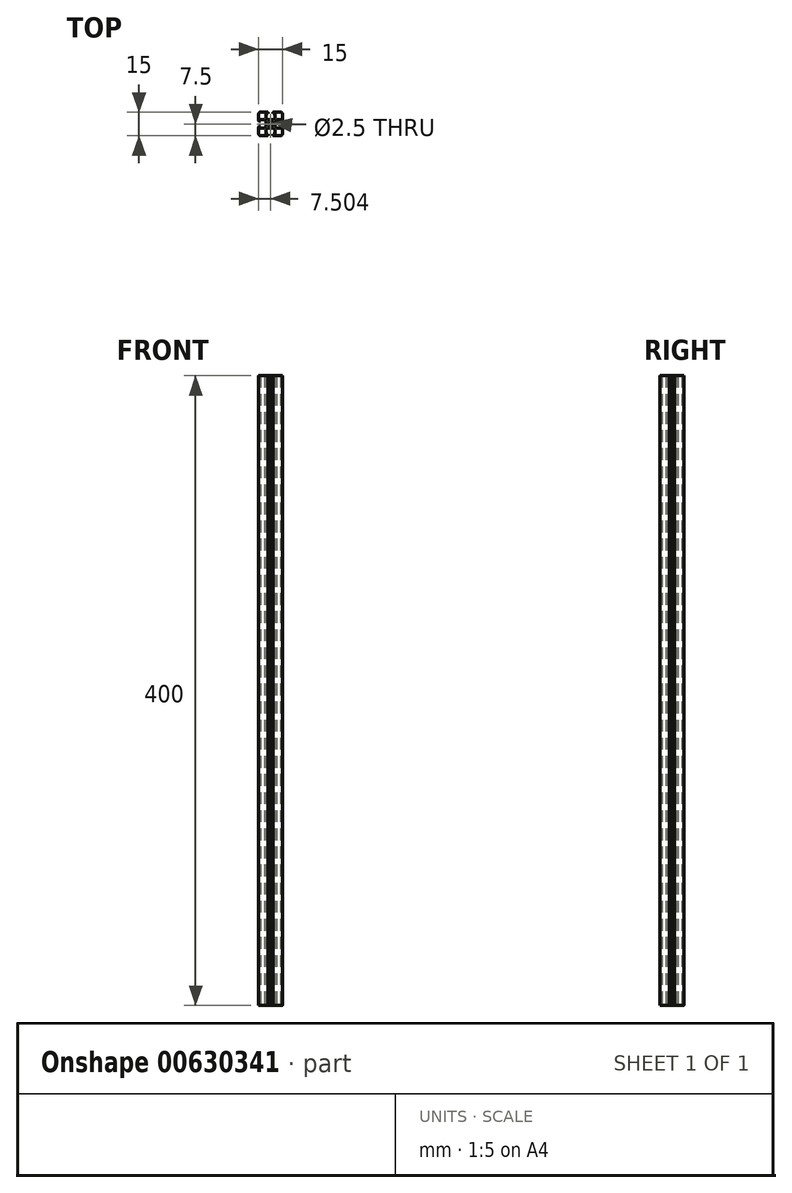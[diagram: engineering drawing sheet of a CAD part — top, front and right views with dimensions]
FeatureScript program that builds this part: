
annotation { "Feature Type Name" : "Feature", "Feature Type Description" : "" }
export const myFeature = defineFeature(function(context is Context, id is Id, definition is map)
    precondition{}
    {
        {
            var Q0;
            Q0=qCreatedBy(makeId("Top.planeOp"),FACE);
            var sketch = newSketch(context, id + "F0", { "sketchPlane" : qUnion([Q0])});
            skLineSegment(sketch, "E0", {"start": v(-5.54, -0.25) * mm, "end": v(-2.91, -0.25) * mm});
            skLineSegment(sketch, "E1", {"start": v(-4.23, -1.56) * mm, "end": v(-4.23, 1.06) * mm});
            skLineSegment(sketch, "E2", {"start": v(-11.73, 6.25) * mm, "end": v(-11.73, 1.75) * mm});
            skArc(sketch, "E3", {"start": v(-11.73, 1.75) * mm, "mid": v(-11.64, 1.54) * mm, "end": v(-11.43, 1.45) * mm});
            skLineSegment(sketch, "E4", {"start": v(-11.43, 1.45) * mm, "end": v(-10.63, 1.45) * mm});
            skLineSegment(sketch, "E5", {"start": v(-10.63, 1.45) * mm, "end": v(-10.63, 2.6) * mm});
            skLineSegment(sketch, "E6", {"start": v(-10.63, 2.6) * mm, "end": v(-8.03, 2.6) * mm});
            skLineSegment(sketch, "E7", {"start": v(-8.03, 2.6) * mm, "end": v(-7.03, 1.6) * mm});
            skLineSegment(sketch, "E8", {"start": v(-7.03, 1.6) * mm, "end": v(-7.03, 0.27) * mm});
            skLineSegment(sketch, "E9", {"start": v(-7.03, 0.27) * mm, "end": v(-6.73, -0.25) * mm});
            skLineSegment(sketch, "E10", {"start": v(-6.73, -0.25) * mm, "end": v(-7.03, -0.77) * mm});
            skLineSegment(sketch, "E11", {"start": v(-7.03, -0.77) * mm, "end": v(-7.03, -2.1) * mm});
            skLineSegment(sketch, "E12", {"start": v(-7.03, -2.1) * mm, "end": v(-8.03, -3.1) * mm});
            skLineSegment(sketch, "E13", {"start": v(-8.03, -3.1) * mm, "end": v(-10.63, -3.1) * mm});
            skLineSegment(sketch, "E14", {"start": v(-10.63, -3.1) * mm, "end": v(-10.63, -1.95) * mm});
            skLineSegment(sketch, "E15", {"start": v(-10.63, -1.95) * mm, "end": v(-11.43, -1.95) * mm});
            skArc(sketch, "E16", {"start": v(-11.43, -1.95) * mm, "mid": v(-11.64, -2.04) * mm, "end": v(-11.73, -2.25) * mm});
            skLineSegment(sketch, "E17", {"start": v(-11.73, -2.25) * mm, "end": v(-11.73, -6.75) * mm});
            skArc(sketch, "E18", {"start": v(-11.73, -6.75) * mm, "mid": v(-11.43, -7.46) * mm, "end": v(-10.73, -7.75) * mm});
            skLineSegment(sketch, "E19", {"start": v(-10.73, -7.75) * mm, "end": v(-6.23, -7.75) * mm});
            skArc(sketch, "E20", {"start": v(-6.23, -7.75) * mm, "mid": v(-6.01, -7.66) * mm, "end": v(-5.93, -7.45) * mm});
            skLineSegment(sketch, "E21", {"start": v(-5.93, -7.45) * mm, "end": v(-5.93, -6.65) * mm});
            skLineSegment(sketch, "E22", {"start": v(-5.93, -6.65) * mm, "end": v(-7.08, -6.65) * mm});
            skLineSegment(sketch, "E23", {"start": v(-7.08, -6.65) * mm, "end": v(-7.08, -4.05) * mm});
            skLineSegment(sketch, "E24", {"start": v(-7.08, -4.05) * mm, "end": v(-6.08, -3.05) * mm});
            skLineSegment(sketch, "E25", {"start": v(-6.08, -3.05) * mm, "end": v(-4.75, -3.05) * mm});
            skLineSegment(sketch, "E26", {"start": v(-4.75, -3.05) * mm, "end": v(-4.23, -2.75) * mm});
            skLineSegment(sketch, "E27", {"start": v(-4.23, -2.75) * mm, "end": v(-3.7, -3.05) * mm});
            skLineSegment(sketch, "E28", {"start": v(-3.7, -3.05) * mm, "end": v(-2.38, -3.05) * mm});
            skLineSegment(sketch, "E29", {"start": v(-2.38, -3.05) * mm, "end": v(-1.38, -4.05) * mm});
            skLineSegment(sketch, "E30", {"start": v(-1.38, -4.05) * mm, "end": v(-1.38, -6.65) * mm});
            skLineSegment(sketch, "E31", {"start": v(-1.38, -6.65) * mm, "end": v(-2.53, -6.65) * mm});
            skLineSegment(sketch, "E32", {"start": v(-2.53, -6.65) * mm, "end": v(-2.53, -7.45) * mm});
            skArc(sketch, "E33", {"start": v(-2.53, -7.45) * mm, "mid": v(-2.44, -7.66) * mm, "end": v(-2.23, -7.75) * mm});
            skLineSegment(sketch, "E34", {"start": v(-2.23, -7.75) * mm, "end": v(2.27, -7.75) * mm});
            skArc(sketch, "E35", {"start": v(2.27, -7.75) * mm, "mid": v(2.98, -7.46) * mm, "end": v(3.27, -6.75) * mm});
            skLineSegment(sketch, "E36", {"start": v(3.27, -6.75) * mm, "end": v(3.27, -2.25) * mm});
            skArc(sketch, "E37", {"start": v(3.27, -2.25) * mm, "mid": v(3.19, -2.04) * mm, "end": v(2.97, -1.95) * mm});
            skLineSegment(sketch, "E38", {"start": v(2.97, -1.95) * mm, "end": v(2.17, -1.95) * mm});
            skLineSegment(sketch, "E39", {"start": v(2.17, -1.95) * mm, "end": v(2.17, -3.1) * mm});
            skLineSegment(sketch, "E40", {"start": v(2.17, -3.1) * mm, "end": v(-0.43, -3.1) * mm});
            skLineSegment(sketch, "E41", {"start": v(-0.43, -3.1) * mm, "end": v(-1.43, -2.1) * mm});
            skLineSegment(sketch, "E42", {"start": v(-1.43, -2.1) * mm, "end": v(-1.43, -0.77) * mm});
            skLineSegment(sketch, "E43", {"start": v(-1.43, -0.77) * mm, "end": v(-1.73, -0.25) * mm});
            skLineSegment(sketch, "E44", {"start": v(-1.73, -0.25) * mm, "end": v(-1.43, 0.27) * mm});
            skLineSegment(sketch, "E45", {"start": v(-1.43, 0.27) * mm, "end": v(-1.43, 1.6) * mm});
            skLineSegment(sketch, "E46", {"start": v(-1.43, 1.6) * mm, "end": v(-0.43, 2.6) * mm});
            skLineSegment(sketch, "E47", {"start": v(-0.43, 2.6) * mm, "end": v(2.17, 2.6) * mm});
            skLineSegment(sketch, "E48", {"start": v(2.17, 2.6) * mm, "end": v(2.17, 1.45) * mm});
            skLineSegment(sketch, "E49", {"start": v(2.17, 1.45) * mm, "end": v(2.97, 1.45) * mm});
            skArc(sketch, "E50", {"start": v(2.97, 1.45) * mm, "mid": v(3.19, 1.54) * mm, "end": v(3.27, 1.75) * mm});
            skLineSegment(sketch, "E51", {"start": v(3.27, 1.75) * mm, "end": v(3.27, 6.25) * mm});
            skArc(sketch, "E52", {"start": v(3.27, 6.25) * mm, "mid": v(2.98, 6.96) * mm, "end": v(2.27, 7.25) * mm});
            skLineSegment(sketch, "E53", {"start": v(2.27, 7.25) * mm, "end": v(-2.23, 7.25) * mm});
            skArc(sketch, "E54", {"start": v(-2.23, 7.25) * mm, "mid": v(-2.44, 7.16) * mm, "end": v(-2.53, 6.95) * mm});
            skLineSegment(sketch, "E55", {"start": v(-2.53, 6.95) * mm, "end": v(-2.53, 6.15) * mm});
            skLineSegment(sketch, "E56", {"start": v(-2.53, 6.15) * mm, "end": v(-1.38, 6.15) * mm});
            skLineSegment(sketch, "E57", {"start": v(-1.38, 6.15) * mm, "end": v(-1.38, 3.55) * mm});
            skLineSegment(sketch, "E58", {"start": v(-1.38, 3.55) * mm, "end": v(-2.38, 2.55) * mm});
            skLineSegment(sketch, "E59", {"start": v(-2.38, 2.55) * mm, "end": v(-3.7, 2.55) * mm});
            skLineSegment(sketch, "E60", {"start": v(-3.7, 2.55) * mm, "end": v(-4.23, 2.25) * mm});
            skLineSegment(sketch, "E61", {"start": v(-4.23, 2.25) * mm, "end": v(-4.75, 2.55) * mm});
            skLineSegment(sketch, "E62", {"start": v(-4.75, 2.55) * mm, "end": v(-6.08, 2.55) * mm});
            skLineSegment(sketch, "E63", {"start": v(-6.08, 2.55) * mm, "end": v(-7.08, 3.55) * mm});
            skLineSegment(sketch, "E64", {"start": v(-7.08, 3.55) * mm, "end": v(-7.08, 6.15) * mm});
            skLineSegment(sketch, "E65", {"start": v(-7.08, 6.15) * mm, "end": v(-5.93, 6.15) * mm});
            skLineSegment(sketch, "E66", {"start": v(-5.93, 6.15) * mm, "end": v(-5.93, 6.95) * mm});
            skArc(sketch, "E67", {"start": v(-5.93, 6.95) * mm, "mid": v(-6.01, 7.16) * mm, "end": v(-6.23, 7.25) * mm});
            skLineSegment(sketch, "E68", {"start": v(-6.23, 7.25) * mm, "end": v(-10.73, 7.25) * mm});
            skCircle(sketch, "E69", {"center": v(-4.23, -0.25) * mm, "radius": 1.25 * mm});
            skArc(sketch, "E70", {"start": v(-10.73, 7.25) * mm, "mid": v(-11.43, 6.96) * mm, "end": v(-11.73, 6.25) * mm});
            skSolve(sketch);
        }
        {
            var Q0;
            Q0=makeQuery(id+"F0.imprint","IMPRINT",FACE,{"disambiguationData":[TD([[makeQuery(id+"F0.imprint","IMPRINT",EDGE,{"derivedFrom":sQuery(id+"F0.wireOp",EDGE,"E2")}),1.0]])]});
            extrude(context, id + "F1", {"entities" : qUnion([Q0]), "depth" : 400 * mm, "offsetDistance" : 25 * mm});
        }
    });
